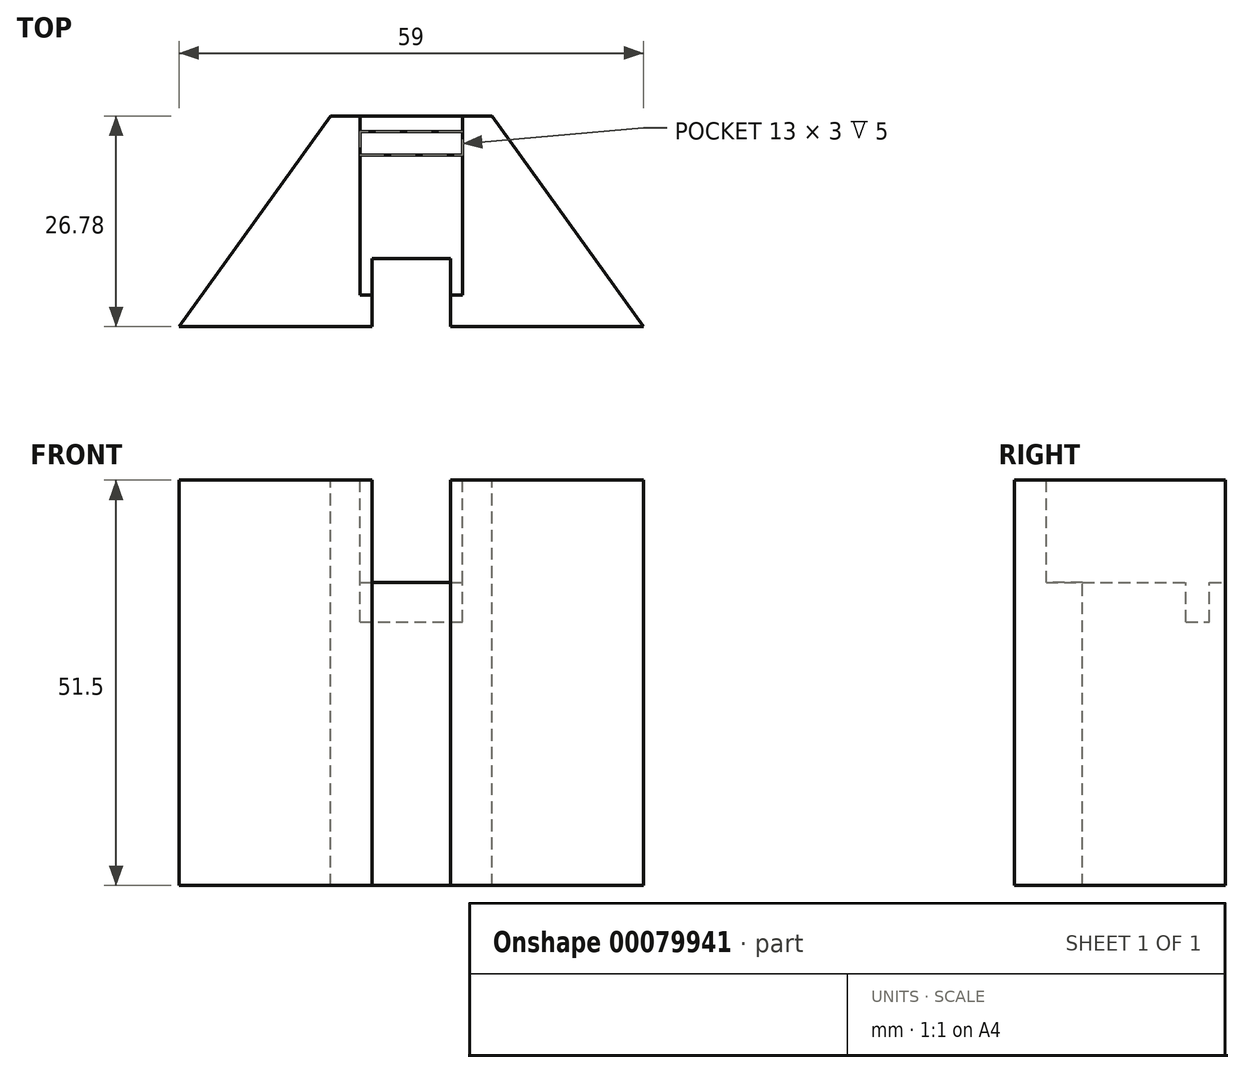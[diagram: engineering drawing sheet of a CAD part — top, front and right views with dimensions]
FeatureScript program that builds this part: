
annotation { "Feature Type Name" : "Feature", "Feature Type Description" : "" }
export const myFeature = defineFeature(function(context is Context, id is Id, definition is map)
    precondition{}
    {
        {
            var Q0;
            Q0=qCreatedBy(makeId("Top.planeOp"),FACE);
            var sketch = newSketch(context, id + "F0", { "sketchPlane" : qUnion([Q0])});
            skLineSegment(sketch, "E0", {"start": v(-29.5, -13.4) * mm, "end": v(-10.25, 13.4) * mm});
            skLineSegment(sketch, "E1", {"start": v(-10.25, 13.4) * mm, "end": v(10.25, 13.4) * mm});
            skLineSegment(sketch, "E2", {"start": v(10.25, 13.4) * mm, "end": v(29.5, -13.4) * mm});
            skLineSegment(sketch, "E3", {"start": v(29.5, -13.4) * mm, "end": v(-29.5, -13.4) * mm});
            skSolve(sketch);
        }
        {
            var Q0;
            Q0=makeQuery(id+"F0.imprint","IMPRINT",FACE,{"disambiguationData":[TD([[makeQuery(id+"F0.imprint","IMPRINT",EDGE,{"derivedFrom":sQuery(id+"F0.wireOp",EDGE,"E0")}),-1.0]])]});
            extrude(context, id + "F1", {"entities" : qUnion([Q0]), "oppositeDirection" : true, "depth" : 51.5 * mm});
        }
        {
            var Q0;
            Q0=makeQuery(id+"F1.opExtrude","SWEPT_FACE",FACE,{"disambiguationData":[OSD([sQuery(id+"F0.wireOp",EDGE,"E1")])]});
            var sketch = newSketch(context, id + "F2", { "sketchPlane" : qUnion([Q0])});
            skLineSegment(sketch, "E4.bottom", {"start": v(6.5, -13) * mm, "end": v(-6.5, -13) * mm});
            skLineSegment(sketch, "E4.top", {"start": v(6.5, 0) * mm, "end": v(-6.5, 0) * mm});
            skLineSegment(sketch, "E4.left", {"start": v(6.5, -13) * mm, "end": v(6.5, 0) * mm});
            skLineSegment(sketch, "E4.right", {"start": v(-6.5, -13) * mm, "end": v(-6.5, 0) * mm});
            skSolve(sketch);
        }
        {
            var Q0;
            Q0=makeQuery(id+"F2.imprint","IMPRINT",FACE,{"disambiguationData":[TD([[makeQuery(id+"F2.imprint","IMPRINT",EDGE,{"derivedFrom":sQuery(id+"F2.wireOp",EDGE,"E4.bottom")}),-1.0]])]});
            extrude(context, id + "F3", {"entities" : qUnion([Q0]), "operationType" : NewBodyOperationType.REMOVE, "oppositeDirection" : true, "depth" : 22.75 * mm});
        }
        {
            var Q0;
            Q0=makeQuery(id+"F3.boolean.opBoolean","COPY",FACE,{"derivedFrom":makeQuery(id+"F3.opExtrude","SWEPT_FACE",FACE,{"disambiguationData":[OSD([sQuery(id+"F2.wireOp",EDGE,"E4.bottom")])]})});
            var sketch = newSketch(context, id + "F4", { "sketchPlane" : qUnion([Q0])});
            skLineSegment(sketch, "E5.bottom", {"start": v(-6.5, 11.4) * mm, "end": v(6.5, 11.4) * mm});
            skLineSegment(sketch, "E5.top", {"start": v(-6.5, 8.4) * mm, "end": v(6.5, 8.4) * mm});
            skLineSegment(sketch, "E5.left", {"start": v(-6.5, 11.4) * mm, "end": v(-6.5, 8.4) * mm});
            skLineSegment(sketch, "E5.right", {"start": v(6.5, 11.4) * mm, "end": v(6.5, 8.4) * mm});
            skSolve(sketch);
        }
        {
            var Q0;
            Q0 = qSketchRegion(id + "F4", true);
            extrude(context, id + "F5", {"entities" : qUnion([Q0]), "operationType" : NewBodyOperationType.REMOVE, "oppositeDirection" : true, "depth" : 5 * mm});
        }
        {
            var Q0;
            Q0=makeQuery(id+"F1.opExtrude","CAP_FACE",FACE,{"disambiguationData":[OSD([sQuery(id+"F0.wireOp",EDGE,"E0"),sQuery(id+"F0.wireOp",EDGE,"E1"),sQuery(id+"F0.wireOp",EDGE,"E2"),sQuery(id+"F0.wireOp",EDGE,"E3")])],"isStart":true});
            var sketch = newSketch(context, id + "F6", { "sketchPlane" : qUnion([Q0])});
            skPoint(sketch, "E6.middle", {"position": v(0, -9.36) * mm});
            skLineSegment(sketch, "E7", {"start": v(-16.37, -13.4) * mm, "end": v(8.27, -13.4) * mm, "construction": true});
            skLineSegment(sketch, "E8.bottom", {"start": v(-5, -4.72) * mm, "end": v(5, -4.72) * mm});
            skLineSegment(sketch, "E8.top", {"start": v(-5, -13.4) * mm, "end": v(5, -13.4) * mm});
            skLineSegment(sketch, "E8.left", {"start": v(-5, -4.72) * mm, "end": v(-5, -13.4) * mm});
            skLineSegment(sketch, "E8.right", {"start": v(5, -4.72) * mm, "end": v(5, -13.4) * mm});
            skSolve(sketch);
        }
        {
            var Q0;
            Q0 = qSketchRegion(id + "F6", true);
            extrude(context, id + "F7", {"entities" : qUnion([Q0]), "operationType" : NewBodyOperationType.REMOVE, "oppositeDirection" : true, "depth" : 51.5 * mm});
        }
    });
